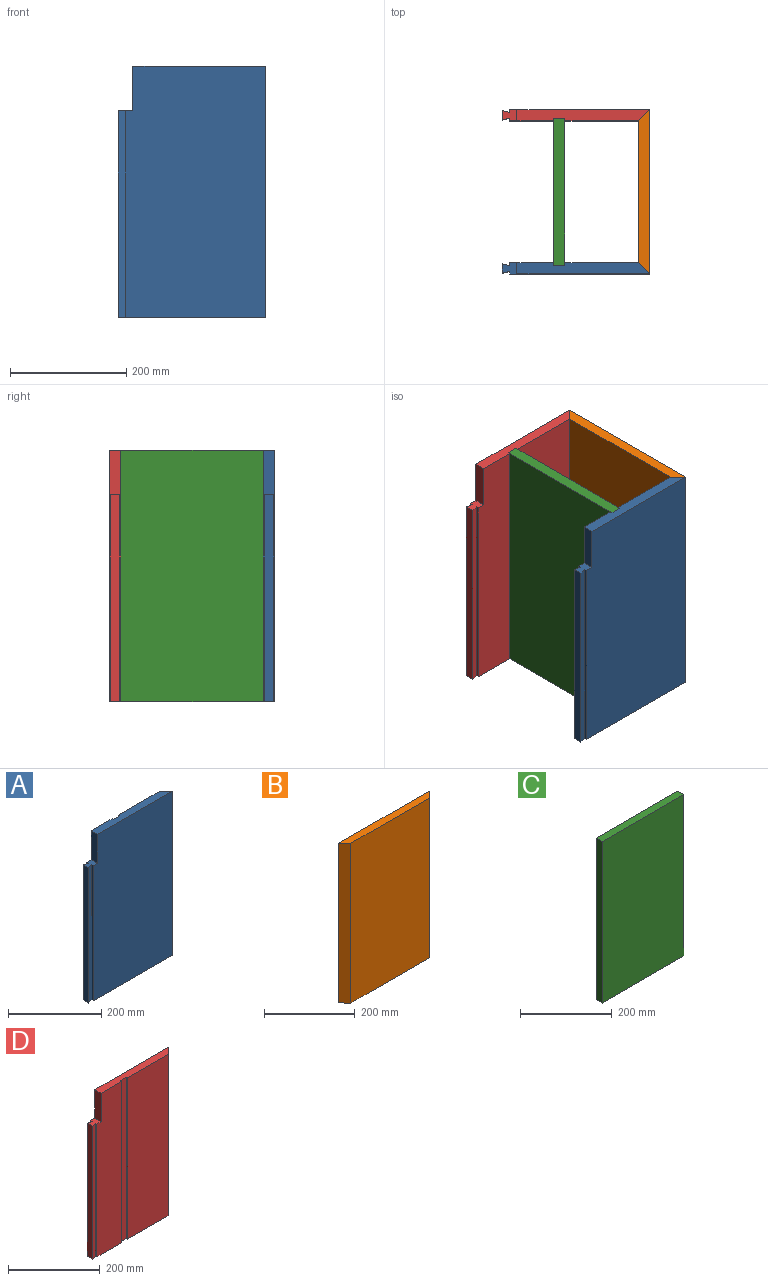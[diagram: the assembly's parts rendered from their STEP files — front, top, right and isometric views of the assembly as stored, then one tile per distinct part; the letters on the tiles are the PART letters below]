
ASSEMBLY  parts=4 mates=3
PART A: 16 faces, bbox 254x19.1x431.8 mm
  f0: plane 228.6x19.05mm, normal (0,0,1), area 4097.8mm2, adj f6,f7,f8,f9,f11,f12,f13,f15
  f1: plane 355.6x4.75mm, normal (-1,0,0), area 1690.5mm2, adj f2,f6,f10,f14
  f2: plane 355.6x12.7mm, normal (0.24,0.97,0), area 4654.4mm2, adj f1,f3,f10,f14
  f3: plane 355.6x15.88mm, normal (-1,0,0), area 5645.2mm2, adj f2,f4,f10,f14
  f4: plane 355.6x12.7mm, normal (0.24,-0.97,0), area 4654.4mm2, adj f3,f5,f10,f14
  f5: plane 355.6x4.75mm, normal (-1,0,0), area 1690.5mm2, adj f4,f8,f10,f14
  f6: plane 431.8x76.2mm, normal (0,1,0), area 31935.4mm2, adj f0,f1,f10,f11,f14,f15
  f7: plane 431.8x127mm, normal (0,1,0), area 54838.6mm2, adj f0,f9,f10,f12
  f8: plane 431.8x241.3mm, normal (0,-1,0), area 103225.6mm2, adj f0,f5,f9,f10,f14,f15
  f9: plane 431.8x19.05mm, normal (0.71,0.71,0), area 11633mm2, adj f0,f7,f8,f10
  f10: plane 254x19.05mm, normal (0,0,-1), area 4501.1mm2, adj f1,f2,f3,f4,f5,f6,f7,f8
  f11: plane 431.8x3.97mm, normal (1,0,0), area 1713.7mm2, adj f0,f6,f10,f13
  f12: plane 431.8x3.97mm, normal (-1,0,0), area 1713.7mm2, adj f0,f7,f10,f13
  f13: plane 431.8x19.05mm, normal (0,1,0), area 8225.8mm2, adj f0,f10,f11,f12
  f14: plane 25.4x19.05mm, normal (0,0,1), area 403.3mm2, adj f1,f2,f3,f4,f5,f6,f8,f15
  f15: plane 76.2x19.05mm, normal (-1,0,0), area 1451.6mm2, adj f0,f6,f8,f14
PART B: 6 faces, bbox 282.6x19.1x431.8 mm
  f0: plane 431.8x282.58mm, normal (0,1,0), area 122015.9mm2, adj f1,f3,f4,f5
  f1: plane 431.8x19.05mm, normal (-0.71,-0.71,0), area 11633mm2, adj f0,f2,f4,f5
  f2: plane 431.8x244.48mm, normal (0,-1,0), area 105564.3mm2, adj f1,f3,f4,f5
  f3: plane 431.8x19.05mm, normal (0.71,-0.71,0), area 11633mm2, adj f0,f2,f4,f5
  f4: plane 282.58x19.05mm, normal (0,0,1), area 5020.2mm2, adj f0,f1,f2,f3
  f5: plane 282.58x19.05mm, normal (0,0,-1), area 5020.2mm2, adj f0,f1,f2,f3
PART C: 6 faces, bbox 252.4x19.1x431.8 mm
  f0: plane 431.8x19.05mm, normal (-1,0,0), area 8225.8mm2, adj f1,f3,f4,f5
  f1: plane 431.8x252.41mm, normal (0,-1,0), area 108991.7mm2, adj f0,f2,f4,f5
  f2: plane 431.8x19.05mm, normal (1,0,0), area 8225.8mm2, adj f1,f3,f4,f5
  f3: plane 431.8x252.41mm, normal (0,1,0), area 108991.7mm2, adj f0,f2,f4,f5
  f4: plane 252.41x19.05mm, normal (0,0,1), area 4808.5mm2, adj f0,f1,f2,f3
  f5: plane 252.41x19.05mm, normal (0,0,-1), area 4808.5mm2, adj f0,f1,f2,f3
PART D: 16 faces, bbox 254x19.1x431.8 mm
  f0: plane 228.6x19.05mm, normal (0,0,1), area 4097.8mm2, adj f2,f3,f8,f9,f11,f12,f13,f14
  f1: plane 355.6x4.75mm, normal (-1,0,0), area 1690.5mm2, adj f2,f7,f10,f15
  f2: plane 431.8x76.2mm, normal (0,-1,0), area 31935.4mm2, adj f0,f1,f10,f11,f14,f15
  f3: plane 431.8x241.3mm, normal (0,1,0), area 103225.6mm2, adj f0,f4,f9,f10,f14,f15
  f4: plane 355.6x4.75mm, normal (-1,0,0), area 1690.5mm2, adj f3,f5,f10,f15
  f5: plane 355.6x12.7mm, normal (0.24,0.97,0), area 4654.4mm2, adj f4,f6,f10,f15
  f6: plane 355.6x15.88mm, normal (-1,0,0), area 5645.2mm2, adj f5,f7,f10,f15
  f7: plane 355.6x12.7mm, normal (0.24,-0.97,0), area 4654.4mm2, adj f1,f6,f10,f15
  f8: plane 431.8x127mm, normal (0,-1,0), area 54838.6mm2, adj f0,f9,f10,f12
  f9: plane 431.8x19.05mm, normal (0.71,-0.71,0), area 11633mm2, adj f0,f3,f8,f10
  f10: plane 254x19.05mm, normal (0,0,-1), area 4501.1mm2, adj f1,f2,f3,f4,f5,f6,f7,f8
  f11: plane 431.8x3.97mm, normal (1,0,0), area 1713.7mm2, adj f0,f2,f10,f13
  f12: plane 431.8x3.97mm, normal (-1,0,0), area 1713.7mm2, adj f0,f8,f10,f13
  f13: plane 431.8x19.05mm, normal (0,-1,0), area 8225.8mm2, adj f0,f10,f11,f12
  f14: plane 76.2x19.05mm, normal (-1,0,0), area 1451.6mm2, adj f0,f2,f3,f15
  f15: plane 25.4x19.05mm, normal (0,0,1), area 403.3mm2, adj f1,f2,f3,f4,f5,f6,f7,f14
PLACE A t=(0,22.46,-25.4)mm
PLACE B rot(axis=(-0.71,-0.71,0),180deg) t=(388.38,-518.46,406.4)mm
PLACE C rot(axis=(0.71,0.71,0),180deg) t=(178.14,-503.38,406.4)mm
PLACE D t=(0,-22.72,-25.4)mm
MATE fastened C.f2 <-> D.f13  axis (0,1,0) through (520.43,88.97,190.5)mm
MATE fastened B.f3 <-> D.f9  axis (-0.71,0.71,0) through (666.48,94.53,190.5)mm
MATE fastened A.f9 <-> B.f1  axis (0.71,0.71,0) through (666.48,-169,190.5)mm
